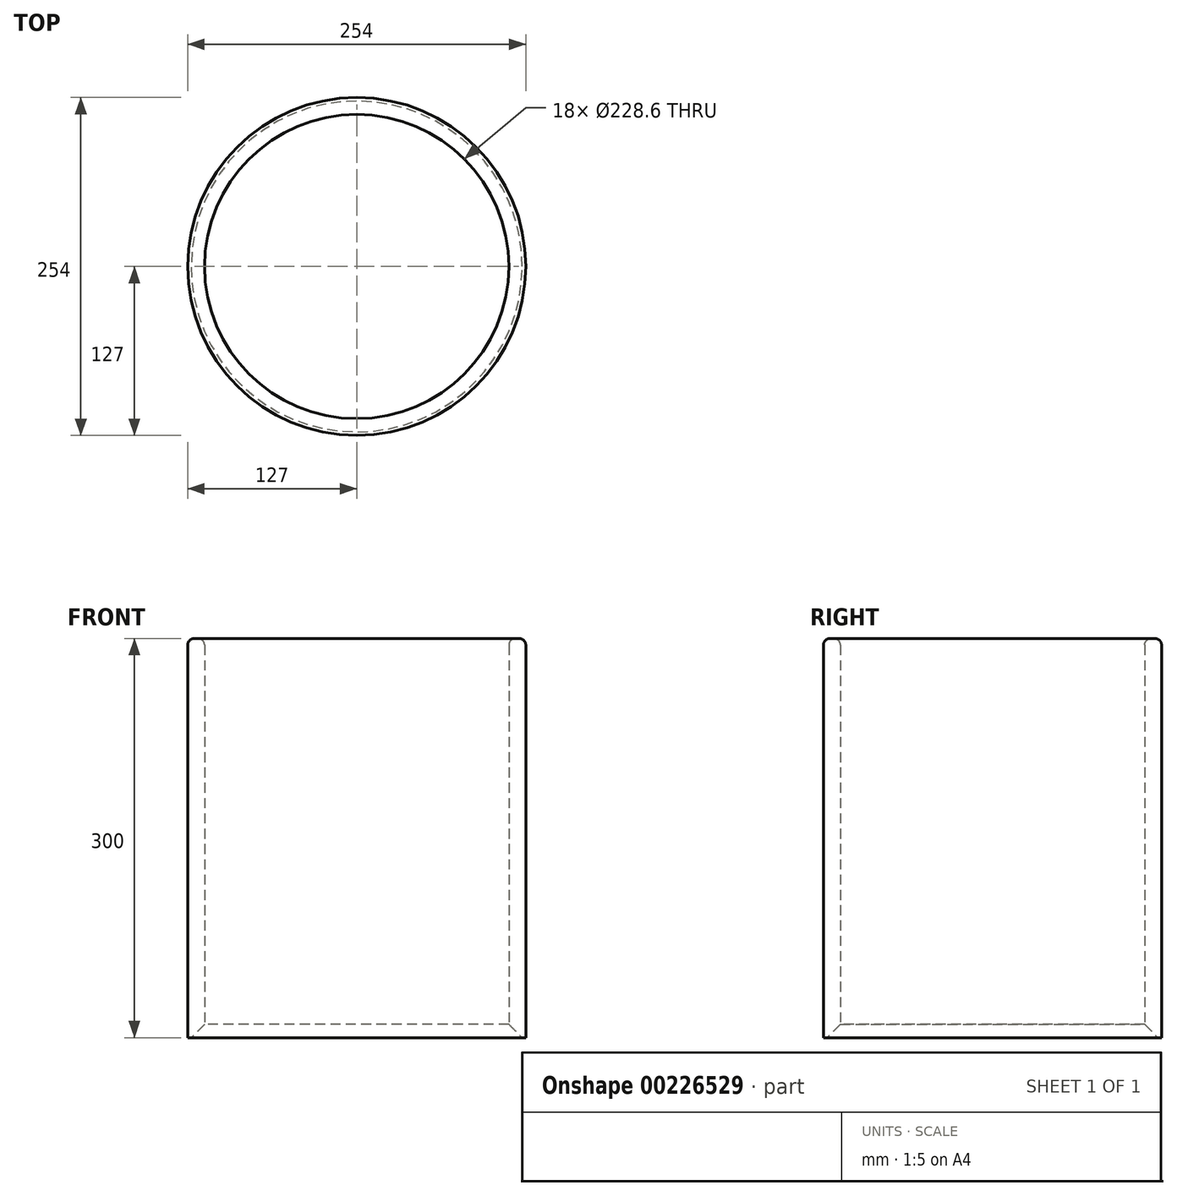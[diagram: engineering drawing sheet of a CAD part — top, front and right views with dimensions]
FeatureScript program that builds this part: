
annotation { "Feature Type Name" : "Feature", "Feature Type Description" : "" }
export const myFeature = defineFeature(function(context is Context, id is Id, definition is map)
    precondition{}
    {
        {
            var Q0;
            Q0=qCreatedBy(makeId("Top.planeOp"),FACE);
            var sketch = newSketch(context, id + "F0", { "sketchPlane" : qUnion([Q0])});
            skCircle(sketch, "E0", {"center": v(0, 0) * mm, "radius": 127 * mm});
            skCircle(sketch, "E1", {"center": v(0, 0) * mm, "radius": 114.3 * mm});
            skSolve(sketch);
        }
        {
            var Q0;
            Q0=makeQuery(id+"F0.imprint","IMPRINT",FACE,{"disambiguationData":[TD([[makeQuery(id+"F0.imprint","IMPRINT",EDGE,{"derivedFrom":sQuery(id+"F0.wireOp",EDGE,"E0")}),1.0]])]});
            extrude(context, id + "F1", {"entities" : qUnion([Q0]), "depth" : 300 * mm});
        }
        {
            var Q0;
            Q0=makeQuery(id+"F1.opExtrude","CAP_FACE",FACE,{"disambiguationData":[OSD([sQuery(id+"F0.wireOp",EDGE,"E0"),sQuery(id+"F0.wireOp",EDGE,"E1")])],"isStart":false});
            fillet(context, id + "F2", {"entities" : qUnion([Q0]), "radius" : 5 * mm, "tangentPropagation" : true, "allowEdgeOverflow" : false});
        }
        {
            var Q0;
            Q0=makeQuery(id+"F1.opExtrude","CAP_EDGE",EDGE,{"disambiguationData":[OSD([sQuery(id+"F0.wireOp",EDGE,"E1")])],"isStart":true});
            chamfer(context, id + "F3", {"entities" : qUnion([Q0]), "width" : 10 * mm, "tangentPropagation" : true});
        }
    });
